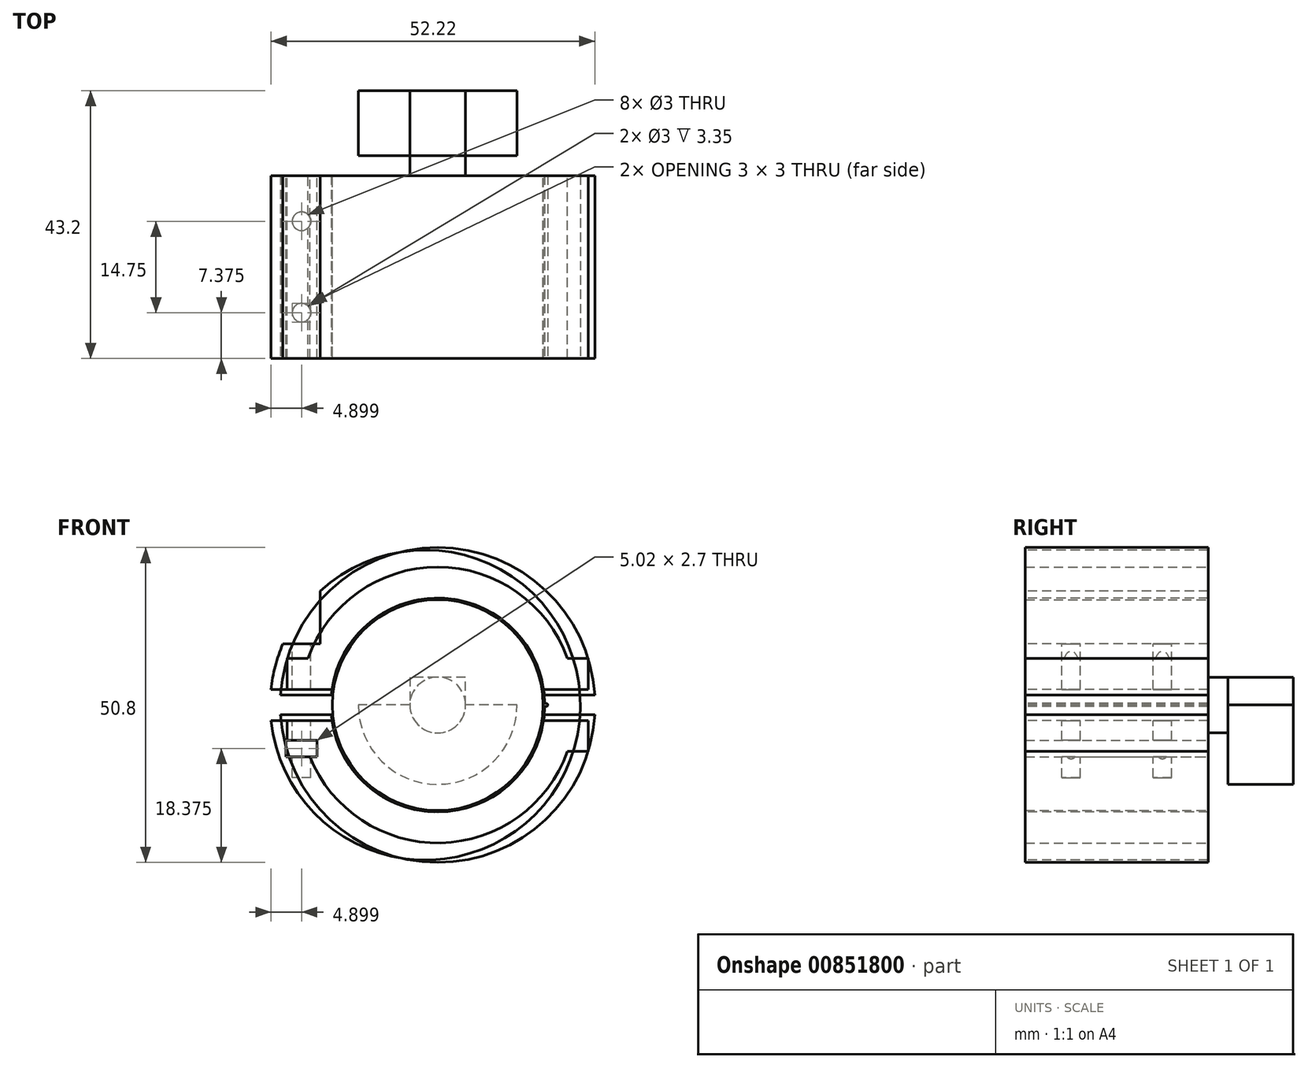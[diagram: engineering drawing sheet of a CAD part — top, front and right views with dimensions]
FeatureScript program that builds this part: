
annotation { "Feature Type Name" : "Feature", "Feature Type Description" : "" }
export const myFeature = defineFeature(function(context is Context, id is Id, definition is map)
    precondition{}
    {
        {
            var Q0;
            Q0=qCreatedBy(makeId("Front.planeOp"),FACE);
            var sketch = newSketch(context, id + "F0", { "sketchPlane" : qUnion([Q0])});
            skCircle(sketch, "E0", {"center": v(0, 0) * mm, "radius": 17 * mm});
            skSolve(sketch);
        }
        {
            var Q0;
            Q0=makeQuery(id+"F0.imprint","IMPRINT",FACE,{"disambiguationData":[TD([[makeQuery(id+"F0.imprint","IMPRINT",EDGE,{"derivedFrom":sQuery(id+"F0.wireOp",EDGE,"E0")}),1.0]])]});
            extrude(context, id + "F1", {"entities" : qUnion([Q0]), "depth" : 29.5 * mm, "offsetDistance" : 25.4 * mm});
        }
        {
            var Q0;
            Q0=makeQuery(id+"F1.opExtrude","CAP_FACE",FACE,{"disambiguationData":[OSD([sQuery(id+"F0.wireOp",EDGE,"E0")])],"isStart":true});
            var sketch = newSketch(context, id + "F2", { "sketchPlane" : qUnion([Q0])});
            skCircle(sketch, "E1", {"center": v(0, 0) * mm, "radius": 4.5 * mm});
            skSolve(sketch);
        }
        {
            var Q0;
            Q0 = qSketchRegion(id + "F2", true);
            extrude(context, id + "F3", {"entities" : qUnion([Q0]), "operationType" : NewBodyOperationType.ADD, "depth" : 13.7 * mm, "offsetDistance" : 25.4 * mm});
        }
        {
            var Q0;
            Q0=makeQuery(id+"F3.opExtrude","CAP_FACE",FACE,{"disambiguationData":[OSD([sQuery(id+"F2.wireOp",EDGE,"E1")])],"isStart":false});
            var sketch = newSketch(context, id + "F4", { "sketchPlane" : qUnion([Q0])});
            skCircle(sketch, "E2", {"center": v(0, 0) * mm, "radius": 12.8 * mm, "construction": true});
            skLineSegment(sketch, "E3.bottom", {"start": v(-4.5, 0) * mm, "end": v(4.5, 0) * mm, "construction": true});
            skLineSegment(sketch, "E3.top", {"start": v(-4.5, 4.5) * mm, "end": v(4.5, 4.5) * mm, "construction": true});
            skLineSegment(sketch, "E3.left", {"start": v(-4.5, 0) * mm, "end": v(-4.5, 4.5) * mm, "construction": true});
            skLineSegment(sketch, "E3.right", {"start": v(4.5, 0) * mm, "end": v(4.5, 4.5) * mm, "construction": true});
            skLineSegment(sketch, "E4", {"start": v(-12.8, 0) * mm, "end": v(-4.5, 0) * mm});
            skLineSegment(sketch, "E5", {"start": v(-4.5, 0) * mm, "end": v(-4.5, 4.5) * mm});
            skLineSegment(sketch, "E6", {"start": v(-4.5, 4.5) * mm, "end": v(4.5, 4.5) * mm});
            skLineSegment(sketch, "E7", {"start": v(4.5, 4.5) * mm, "end": v(4.5, 0) * mm});
            skLineSegment(sketch, "E8", {"start": v(4.5, 0) * mm, "end": v(12.8, 0) * mm});
            skArc(sketch, "E9", {"start": v(-12.8, 0) * mm, "mid": v(0, -12.8) * mm, "end": v(12.8, 0) * mm});
            skSolve(sketch);
        }
        {
            var Q0;
            Q0 = qSketchRegion(id + "F4", true);
            extrude(context, id + "F5", {"entities" : qUnion([Q0]), "operationType" : NewBodyOperationType.ADD, "oppositeDirection" : true, "depth" : 10.5 * mm, "offsetDistance" : 25.4 * mm});
        }
        {
            var Q0;
            Q0=makeQuery(id+"F1.opExtrude","CAP_FACE",FACE,{"disambiguationData":[OSD([sQuery(id+"F0.wireOp",EDGE,"E0")])],"isStart":true});
            var sketch = newSketch(context, id + "F6", { "sketchPlane" : qUnion([Q0])});
            skCircle(sketch, "E10", {"center": v(0, 0) * mm, "radius": 17.25 * mm, "construction": true});
            skLineSegment(sketch, "E11.bottom", {"start": v(-24.27, 2.5) * mm, "end": v(24.27, 2.5) * mm, "construction": true});
            skLineSegment(sketch, "E11.top", {"start": v(-24.27, -2.5) * mm, "end": v(24.27, -2.5) * mm, "construction": true});
            skLineSegment(sketch, "E11.left", {"start": v(-24.27, 2.5) * mm, "end": v(-24.27, -2.5) * mm, "construction": true});
            skLineSegment(sketch, "E11.right", {"start": v(24.27, 2.5) * mm, "end": v(24.27, -2.5) * mm, "construction": true});
            skPoint(sketch, "E12", {"position": v(24.27, 0) * mm});
            skPoint(sketch, "E13", {"position": v(0, 2.5) * mm});
            skLineSegment(sketch, "E14", {"start": v(-24.27, 2.5) * mm, "end": v(-17.07, 2.5) * mm});
            skArc(sketch, "E15", {"start": v(17.07, 2.5) * mm, "mid": v(0, 17.25) * mm, "end": v(-17.07, 2.5) * mm});
            skLineSegment(sketch, "E16", {"start": v(17.07, 2.5) * mm, "end": v(24.27, 2.5) * mm});
            skLineSegment(sketch, "E17.0", {"start": v(20.95, 7.5) * mm, "end": v(24.27, 7.5) * mm});
            skArc(sketch, "E17.1", {"start": v(20.95, 7.5) * mm, "mid": v(0, 22.25) * mm, "end": v(-20.95, 7.5) * mm});
            skLineSegment(sketch, "E17.2", {"start": v(-24.27, 7.5) * mm, "end": v(-20.95, 7.5) * mm});
            skLineSegment(sketch, "E18", {"start": v(-24.27, 2.5) * mm, "end": v(-24.27, 7.5) * mm});
            skLineSegment(sketch, "E19.MirrorCS", {"start": v(24.27, 2.5) * mm, "end": v(24.27, 7.5) * mm});
            skLineSegment(sketch, "E20.MirrorCS", {"start": v(17.07, -2.5) * mm, "end": v(24.27, -2.5) * mm});
            skLineSegment(sketch, "E21.MirrorCS", {"start": v(-24.27, -2.5) * mm, "end": v(-17.07, -2.5) * mm});
            skLineSegment(sketch, "E22.MirrorCS", {"start": v(24.27, -2.5) * mm, "end": v(24.27, -7.5) * mm});
            skLineSegment(sketch, "E23.MirrorCS", {"start": v(-24.27, -7.5) * mm, "end": v(-20.95, -7.5) * mm});
            skArc(sketch, "E24.MirrorCS", {"start": v(20.95, -7.5) * mm, "mid": v(0, -22.25) * mm, "end": v(-20.95, -7.5) * mm});
            skArc(sketch, "E25.MirrorCS", {"start": v(17.07, -2.5) * mm, "mid": v(0, -17.25) * mm, "end": v(-17.07, -2.5) * mm});
            skPoint(sketch, "E26.MirrorP", {"position": v(0, -2.5) * mm});
            skLineSegment(sketch, "E27.MirrorCS", {"start": v(20.95, -7.5) * mm, "end": v(24.27, -7.5) * mm});
            skLineSegment(sketch, "E28.MirrorCS", {"start": v(-24.27, -2.5) * mm, "end": v(-24.27, -7.5) * mm});
            skCircle(sketch, "E29", {"center": v(0, 0) * mm, "radius": 25.4 * mm, "construction": true});
            skSolve(sketch);
        }
        {
            var Q0;
            Q0 = qSketchRegion(id + "F6", true);
            var Q1;
            Q1=makeQuery(id+"F1.opExtrude","CAP_FACE",FACE,{"disambiguationData":[OSD([sQuery(id+"F0.wireOp",EDGE,"E0")])],"isStart":false});
            extrude(context, id + "F7", {"entities" : qUnion([Q0]), "endBound" : BoundingType.UP_TO_SURFACE, "oppositeDirection" : true, "depth" : 25.4 * mm, "endBoundEntityFace" : qUnion([Q1]), "offsetDistance" : 25.4 * mm});
        }
        {
            var Q0;
            Q0=makeQuery(id+"F1.opExtrude","CAP_FACE",FACE,{"disambiguationData":[OSD([sQuery(id+"F0.wireOp",EDGE,"E0")])],"isStart":false});
            var sketch = newSketch(context, id + "F8", { "sketchPlane" : qUnion([Q0])});
            skArc(sketch, "E30", {"start": v(-26.87, -2.5) * mm, "mid": v(21.38, -8.86) * mm, "end": v(-18.97, 18.36) * mm});
            skArc(sketch, "E31", {"start": v(-17.07, -2.5) * mm, "mid": v(1.13, -17.21) * mm, "end": v(17.25, -0.25) * mm});
            skLineSegment(sketch, "E32", {"start": v(-17.07, 2.5) * mm, "end": v(-26.87, 2.5) * mm});
            skLineSegment(sketch, "E33.MirrorCS", {"start": v(-17.07, -2.5) * mm, "end": v(-26.87, -2.5) * mm});
            skLineSegment(sketch, "E34", {"start": v(-24.97, 9.87) * mm, "end": v(-18.97, 9.87) * mm});
            skLineSegment(sketch, "E35", {"start": v(-18.97, 9.87) * mm, "end": v(-18.97, 18.36) * mm});
            skPoint(sketch, "E36", {"position": v(-21.97, 9.87) * mm});
            skPoint(sketch, "E37", {"position": v(-21.97, 2.5) * mm});
            skLineSegment(sketch, "E38", {"start": v(-21.97, 2.5) * mm, "end": v(-21.97, 19.46) * mm, "construction": true});
            skArc(sketch, "E39.trimOffspring", {"start": v(-24.97, 9.87) * mm, "mid": v(-26.2, 6.26) * mm, "end": v(-26.87, 2.5) * mm});
            skLineSegment(sketch, "E40", {"start": v(17.25, 0.25) * mm, "end": v(17.5, 0.25) * mm});
            skLineSegment(sketch, "E41", {"start": v(17.75, 0) * mm, "end": v(17.75, 0) * mm});
            skLineSegment(sketch, "E42.MirrorCS", {"start": v(17.25, -0.25) * mm, "end": v(17.5, -0.25) * mm});
            skArc(sketch, "E43.trimOffspring", {"start": v(17.25, 0.25) * mm, "mid": v(1.13, 17.21) * mm, "end": v(-17.07, 2.5) * mm});
            skPoint(sketch, "E44.visualSharp", {"position": v(17.75, 0.25) * mm});
            skArc(sketch, "E44.filletArc", {"start": v(17.75, 0) * mm, "mid": v(17.67, 0.18) * mm, "end": v(17.5, 0.25) * mm});
            skPoint(sketch, "E45.visualSharp", {"position": v(17.75, -0.25) * mm});
            skArc(sketch, "E45.filletArc", {"start": v(17.5, -0.25) * mm, "mid": v(17.67, -0.18) * mm, "end": v(17.75, 0) * mm});
            skSolve(sketch);
        }
        {
            var Q0;
            Q0 = qSketchRegion(id + "F8", true);
            var Q1;
            Q1=makeQuery(id+"F1.opExtrude","CAP_FACE",FACE,{"disambiguationData":[OSD([sQuery(id+"F0.wireOp",EDGE,"E0")])],"isStart":true});
            extrude(context, id + "F9", {"entities" : qUnion([Q0]), "endBound" : BoundingType.UP_TO_SURFACE, "oppositeDirection" : true, "depth" : 25.4 * mm, "endBoundEntityFace" : qUnion([Q1]), "offsetDistance" : 25.4 * mm});
        }
        {
            var Q0;
            Q0=makeQuery(id+"F9.opExtrude","SWEPT_FACE",FACE,{"disambiguationData":[OSD([sQuery(id+"F8.wireOp",EDGE,"E34")])]});
            var sketch = newSketch(context, id + "F10", { "sketchPlane" : qUnion([Q0])});
            skLineSegment(sketch, "E46", {"start": v(-21.97, 0) * mm, "end": v(-21.97, -14.75) * mm, "construction": true});
            skCircle(sketch, "E47", {"center": v(-21.97, -7.38) * mm, "radius": 1.5 * mm});
            skPoint(sketch, "E48", {"position": v(-21.97, -14.75) * mm});
            skLineSegment(sketch, "E49", {"start": v(-21.97, -14.75) * mm, "end": v(-24.97, -14.75) * mm, "construction": true});
            skCircle(sketch, "E50.MirrorC", {"center": v(-21.97, -22.13) * mm, "radius": 1.5 * mm});
            skPoint(sketch, "E51.orphan", {"position": v(-21.97, -29.5) * mm});
            skSolve(sketch);
        }
        {
            var Q0;
            Q0 = qSketchRegion(id + "F10", true);
            extrude(context, id + "F11", {"entities" : qUnion([Q0]), "operationType" : NewBodyOperationType.REMOVE, "oppositeDirection" : true, "depth" : 21.59 * mm, "offsetDistance" : 25.4 * mm});
        }
        {
            var Q0;
            Q0=makeQuery(id+"F9.opExtrude","CAP_FACE",FACE,{"disambiguationData":[OSD([sQuery(id+"F8.wireOp",EDGE,"E30"),sQuery(id+"F8.wireOp",EDGE,"E31"),sQuery(id+"F8.wireOp",EDGE,"E32"),sQuery(id+"F8.wireOp",EDGE,"E33.MirrorCS"),sQuery(id+"F8.wireOp",EDGE,"E34"),sQuery(id+"F8.wireOp",EDGE,"E35"),sQuery(id+"F8.wireOp",EDGE,"E39.trimOffspring"),sQuery(id+"F8.wireOp",EDGE,"E40"),sQuery(id+"F8.wireOp",EDGE,"E41"),sQuery(id+"F8.wireOp",EDGE,"E42.MirrorCS"),sQuery(id+"F8.wireOp",EDGE,"E41"),sQuery(id+"F8.wireOp",EDGE,"E43.trimOffspring")])],"isStart":false});
            var sketch = newSketch(context, id + "F12", { "sketchPlane" : qUnion([Q0])});
            skPoint(sketch, "E52", {"position": v(21.97, -2.5) * mm});
            skLineSegment(sketch, "E53", {"start": v(21.97, -2.5) * mm, "end": v(21.97, -17.79) * mm, "construction": true});
            skLineSegment(sketch, "E54.bottom", {"start": v(19.46, -5.67) * mm, "end": v(24.48, -5.67) * mm});
            skLineSegment(sketch, "E54.top", {"start": v(19.46, -8.38) * mm, "end": v(24.48, -8.38) * mm});
            skLineSegment(sketch, "E54.left", {"start": v(19.46, -5.68) * mm, "end": v(19.46, -8.38) * mm});
            skLineSegment(sketch, "E54.right", {"start": v(24.48, -5.68) * mm, "end": v(24.48, -8.38) * mm});
            skPoint(sketch, "E55", {"position": v(21.97, -5.68) * mm});
            skLineSegment(sketch, "E56", {"start": v(24.48, -5.68) * mm, "end": v(24.48, -2.5) * mm, "construction": true});
            skSolve(sketch);
        }
        {
            var Q0;
            Q0 = qSketchRegion(id + "F12", true);
            var Q1;
            Q1=makeQuery(id+"F9.opExtrude","CAP_FACE",FACE,{"disambiguationData":[OSD([sQuery(id+"F8.wireOp",EDGE,"E30"),sQuery(id+"F8.wireOp",EDGE,"E31"),sQuery(id+"F8.wireOp",EDGE,"E32"),sQuery(id+"F8.wireOp",EDGE,"E33.MirrorCS"),sQuery(id+"F8.wireOp",EDGE,"E34"),sQuery(id+"F8.wireOp",EDGE,"E35"),sQuery(id+"F8.wireOp",EDGE,"E39.trimOffspring"),sQuery(id+"F8.wireOp",EDGE,"E40"),sQuery(id+"F8.wireOp",EDGE,"E41"),sQuery(id+"F8.wireOp",EDGE,"E42.MirrorCS"),sQuery(id+"F8.wireOp",EDGE,"E41"),sQuery(id+"F8.wireOp",EDGE,"E43.trimOffspring")])],"isStart":true});
            extrude(context, id + "F13", {"entities" : qUnion([Q0]), "operationType" : NewBodyOperationType.REMOVE, "endBound" : BoundingType.UP_TO_SURFACE, "oppositeDirection" : true, "depth" : 25.4 * mm, "endBoundEntityFace" : qUnion([Q1]), "offsetDistance" : 25.4 * mm});
        }
        {
            var Q0;
            Q0=makeQuery(id+"F1.opExtrude","CAP_FACE",FACE,{"disambiguationData":[OSD([sQuery(id+"F0.wireOp",EDGE,"E0")])],"isStart":false});
            var sketch = newSketch(context, id + "F14", { "sketchPlane" : qUnion([Q0])});
            skArc(sketch, "E57", {"start": v(-25.35, -1.59) * mm, "mid": v(0, -25.4) * mm, "end": v(25.35, -1.59) * mm, "construction": true});
            skCircle(sketch, "E58", {"center": v(0, 0) * mm, "radius": 17.25 * mm, "construction": true});
            skLineSegment(sketch, "E59", {"start": v(-17.18, 1.59) * mm, "end": v(-25.35, 1.59) * mm});
            skLineSegment(sketch, "E60.MirrorCS", {"start": v(-17.18, -1.59) * mm, "end": v(-25.35, -1.59) * mm});
            skLineSegment(sketch, "E61.MirrorCS", {"start": v(17.18, 1.59) * mm, "end": v(25.35, 1.59) * mm});
            skLineSegment(sketch, "E62.MirrorCS", {"start": v(17.18, -1.59) * mm, "end": v(25.35, -1.59) * mm});
            skArc(sketch, "E63", {"start": v(25.35, 1.59) * mm, "mid": v(0, 25.4) * mm, "end": v(-25.35, 1.59) * mm});
            skArc(sketch, "E64", {"start": v(17.18, 1.59) * mm, "mid": v(0, 17.25) * mm, "end": v(-17.18, 1.59) * mm});
            skArc(sketch, "E65.MirrorCS", {"start": v(25.35, -1.59) * mm, "mid": v(0, -25.4) * mm, "end": v(-25.35, -1.59) * mm});
            skArc(sketch, "E66.MirrorCS", {"start": v(17.18, -1.59) * mm, "mid": v(0, -17.25) * mm, "end": v(-17.18, -1.59) * mm});
            skArc(sketch, "E67.MirrorC", {"start": v(-25.35, 1.59) * mm, "mid": v(0, 25.4) * mm, "end": v(25.35, 1.59) * mm, "construction": true});
            skArc(sketch, "E68.trimOffspring", {"start": v(25.35, -1.59) * mm, "mid": v(0, -25.4) * mm, "end": v(-25.35, -1.59) * mm, "construction": true});
            skArc(sketch, "E69.trimOffspring", {"start": v(25.35, 1.59) * mm, "mid": v(0, 25.4) * mm, "end": v(-25.35, 1.59) * mm, "construction": true});
            skSolve(sketch);
        }
        {
            var Q0;
            Q0 = qSketchRegion(id + "F14", true);
            var Q1;
            Q1=makeQuery(id+"F1.opExtrude","CAP_FACE",FACE,{"disambiguationData":[OSD([sQuery(id+"F0.wireOp",EDGE,"E0")])],"isStart":true});
            extrude(context, id + "F15", {"entities" : qUnion([Q0]), "endBound" : BoundingType.UP_TO_SURFACE, "oppositeDirection" : true, "depth" : 25.4 * mm, "endBoundEntityFace" : qUnion([Q1]), "offsetDistance" : 25.4 * mm});
        }
    });
